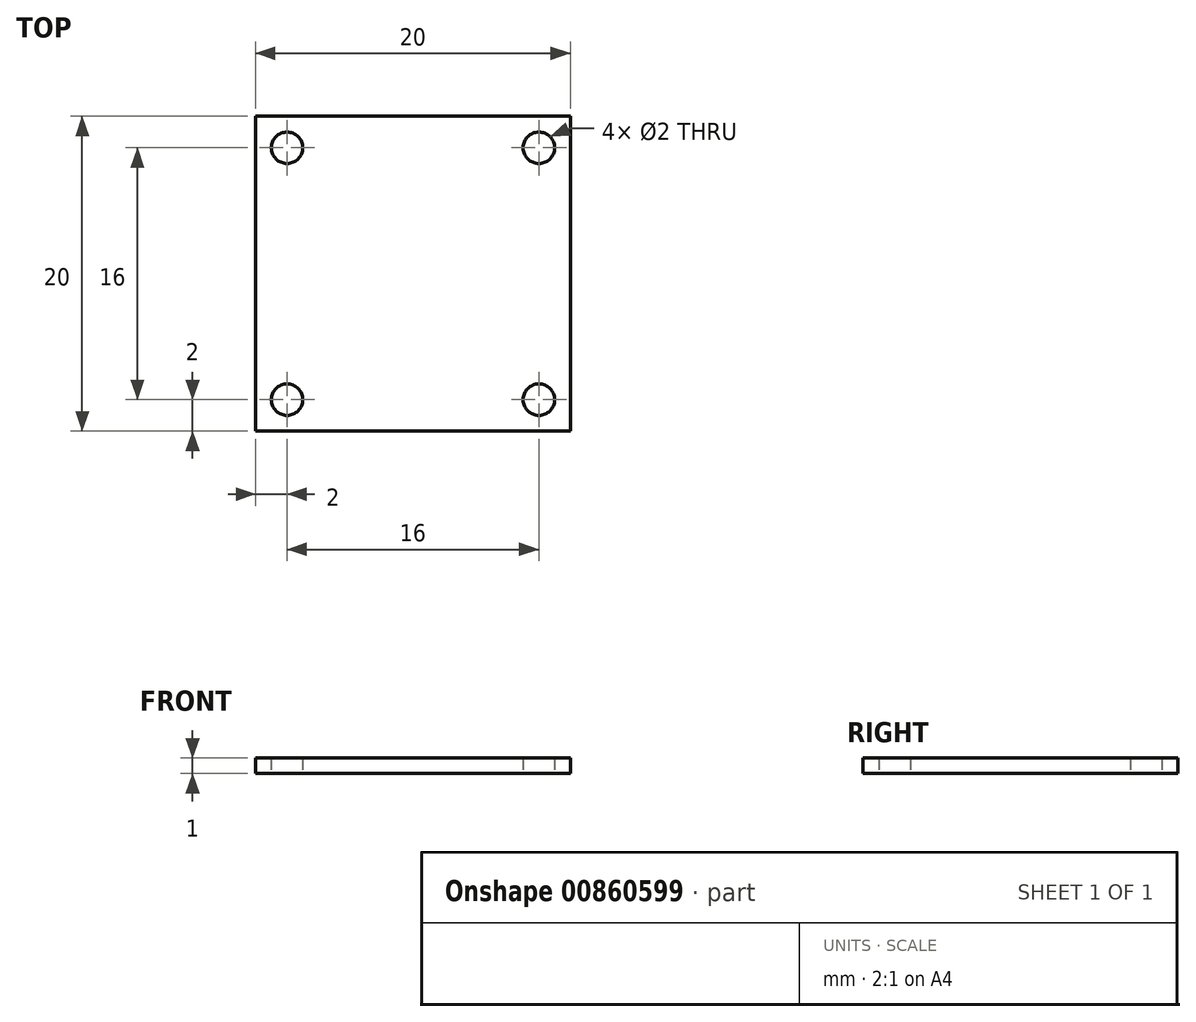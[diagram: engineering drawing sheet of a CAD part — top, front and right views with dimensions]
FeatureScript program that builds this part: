
annotation { "Feature Type Name" : "Feature", "Feature Type Description" : "" }
export const myFeature = defineFeature(function(context is Context, id is Id, definition is map)
    precondition{}
    {
        {
            var Q0;
            Q0=qCreatedBy(makeId("Top.planeOp"),FACE);
            var sketch = newSketch(context, id + "F0", { "sketchPlane" : qUnion([Q0])});
            skCircle(sketch, "E0", {"center": v(-8, 8) * mm, "radius": 1 * mm});
            skCircle(sketch, "E1.0.1.0", {"center": v(-8, -8) * mm, "radius": 1 * mm});
            skCircle(sketch, "E1.1.0.0", {"center": v(8, 8) * mm, "radius": 1 * mm});
            skCircle(sketch, "E1.1.1.0", {"center": v(8, -8) * mm, "radius": 1 * mm});
            skLineSegment(sketch, "E1.direction1", {"start": v(-8, 8) * mm, "end": v(8, 8) * mm, "construction": true});
            skLineSegment(sketch, "E1.direction2", {"start": v(-8, 8) * mm, "end": v(-8, -8) * mm, "construction": true});
            skLineSegment(sketch, "E2.bottom", {"start": v(10, -10) * mm, "end": v(-10, -10) * mm});
            skLineSegment(sketch, "E2.top", {"start": v(10, 10) * mm, "end": v(-10, 10) * mm});
            skLineSegment(sketch, "E2.left", {"start": v(10, -10) * mm, "end": v(10, 10) * mm});
            skLineSegment(sketch, "E2.right", {"start": v(-10, -10) * mm, "end": v(-10, 10) * mm});
            skPoint(sketch, "E2.middle", {"position": v(0, 0) * mm});
            skSolve(sketch);
        }
        {
            var Q0;
            Q0 = qSketchRegion(id + "F0", true);
            extrude(context, id + "F1", {"entities" : qUnion([Q0]), "depth" : 1 * mm, "offsetDistance" : 25 * mm});
        }
    });
